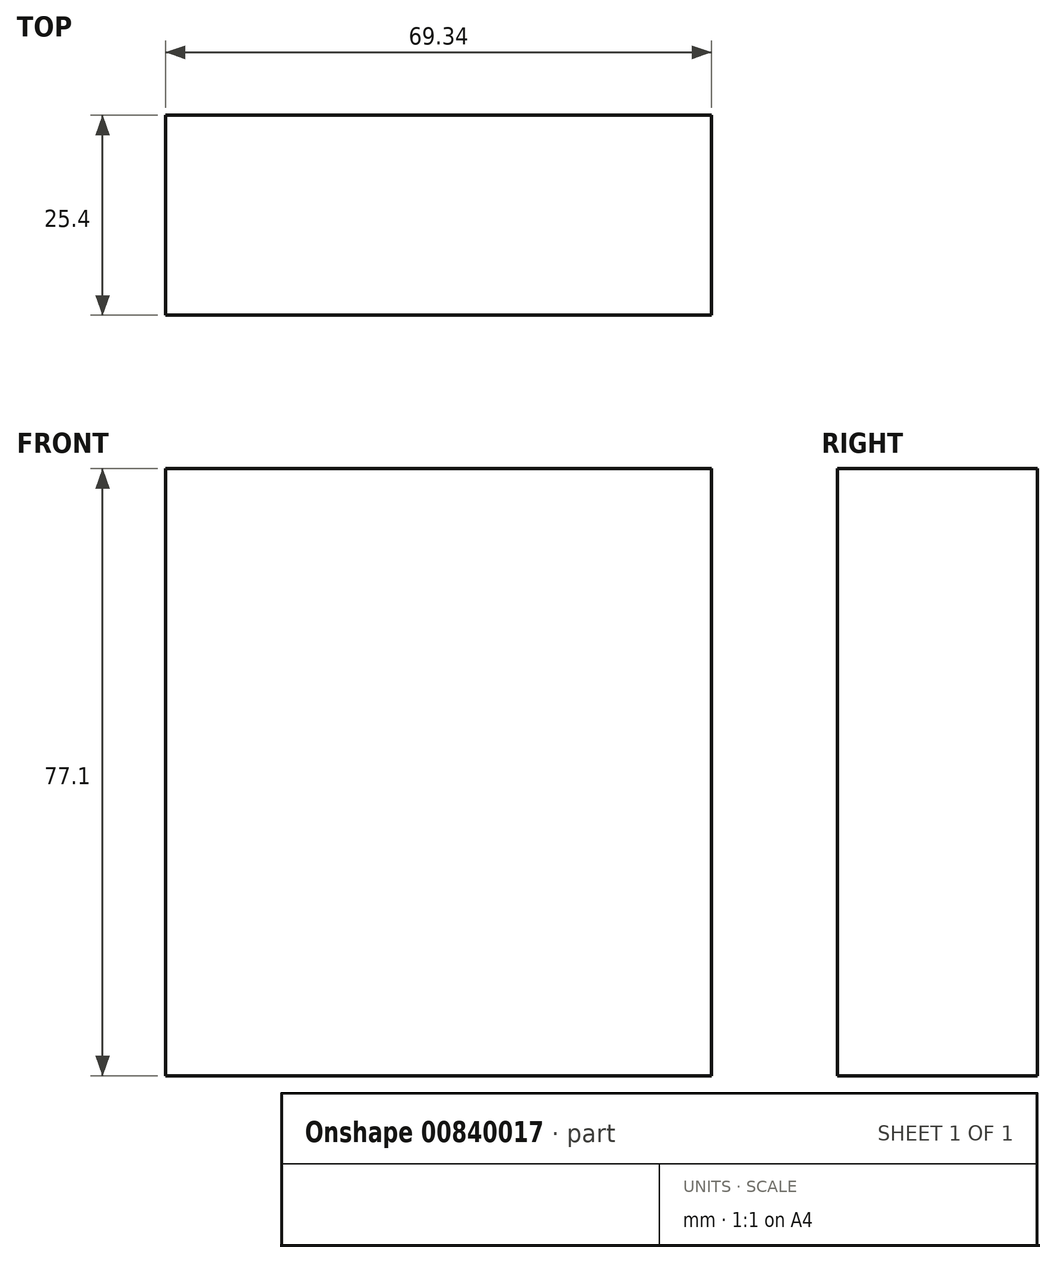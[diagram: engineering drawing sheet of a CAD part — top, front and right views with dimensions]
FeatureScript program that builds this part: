
annotation { "Feature Type Name" : "Feature", "Feature Type Description" : "" }
export const myFeature = defineFeature(function(context is Context, id is Id, definition is map)
    precondition{}
    {
        {
            var Q0;
            Q0=qCreatedBy(makeId("Front.planeOp"),FACE);
            var sketch = newSketch(context, id + "F0", { "sketchPlane" : qUnion([Q0])});
            skLineSegment(sketch, "E0.bottom", {"start": v(46.6, 38.55) * mm, "end": v(-22.73, 38.55) * mm});
            skLineSegment(sketch, "E0.top", {"start": v(46.6, -38.55) * mm, "end": v(-22.73, -38.55) * mm});
            skLineSegment(sketch, "E0.left", {"start": v(46.6, 38.55) * mm, "end": v(46.6, -38.55) * mm});
            skLineSegment(sketch, "E0.right", {"start": v(-22.73, 38.55) * mm, "end": v(-22.73, -38.55) * mm});
            skPoint(sketch, "E0.middle", {"position": v(11.94, 0) * mm});
            skSolve(sketch);
        }
        {
            var Q0;
            Q0=makeQuery(id+"F0.imprint","IMPRINT",FACE,{"disambiguationData":[TD([[makeQuery(id+"F0.imprint","IMPRINT",EDGE,{"derivedFrom":sQuery(id+"F0.wireOp",EDGE,"E0.bottom")}),1.0]])]});
            extrude(context, id + "F1", {"entities" : qUnion([Q0]), "depth" : 25.4 * mm, "offsetDistance" : 25.4 * mm});
        }
    });
